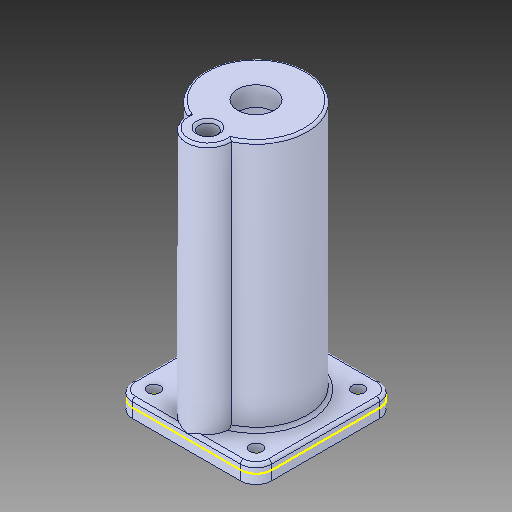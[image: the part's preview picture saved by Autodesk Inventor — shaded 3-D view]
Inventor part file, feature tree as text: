
AUTODESK INVENTOR PART (.ipt)
format: ipt  version: 2018 (Build 220112000, 112)  size: 358,912 bytes
history: native  units: in
note: dims shown in document units (in); Inventor stores cm internally (conversion verified against a paired STEP export)
features: extrude x16, sketch x13, projected_geometry x13, fillet x6, chamfer x1, revolve x1, other x1
ambient origin geometry x8: Origin, YZ Plane, XZ Plane, XY Plane, X Axis, Y Axis, Z Axis, Center Point
bodies: Solid1 (feature_tree)
feature tree (51):
  extrude  "Extrusion1"  TaperAngle=0.0deg  [1 undecoded]
  sketch  "Sketch2"  dims[d4=0.3937in d5=0.0in d6=1.0in d7=0.0in]
  extrude  "Extrusion2"  Depth=1.0in TaperAngle=0.0deg
  extrude  "Extrusion3"  Depth=0.9252in
  sketch  "Sketch3"  dims[d8=2.0in d9=0.0in d10=0.9252in]
  extrude  "Extrusion4"  Depth=2.0in TaperAngle=0.0deg
  extrude  "Extrusion5"  Depth=1.0in
  extrude  "Extrusion6"  Depth=0.3937in TaperAngle=0.0deg
  fillet  "Fillet2"  Radius=0.3937in
  fillet  "Fillet3"  Radius=0.45in
  sketch  "Sketch5"  dims[d14=0.5in d15=1.0in]
  extrude  "Extrusion7"  Depth=0.125in
  extrude  "Extrusion9"  TaperAngle=0.0deg  [1 undecoded]
  extrude  "Extrusion10"  Depth=0.9375in
  fillet  "Fillet4"  Radius=0.5in
  extrude  "Extrusion11"  Depth=0.0625in TaperAngle=45.0deg
  sketch  "Sketch9"  dims[d27=0.0in d28=0.0in d29=0.0in d30=0.0in]
  extrude  "Extrusion12"  Depth=0.25in TaperAngle=0.0deg
  extrude  "Extrusion13"  Depth=0.25in TaperAngle=0.0deg
  extrude  "Extrusion14"  Depth=1.374in
  fillet  "Fillet5"  [1 undecoded]
  chamfer  "Chamfer2"  [1 undecoded]
  fillet  "Fillet6"  [1 undecoded]
  sketch  "Sketch13"  dims[d46=0.25in d47=0.0in d48=0.25in d49=0.0in]
  extrude  "Extrusion15"  [1 undecoded]
  extrude  "Extrusion16"  [1 undecoded]
  extrude  "Extrusion17"  [1 undecoded]
  revolve  "Revolution1"  [1 undecoded]
  fillet  "Fillet1"  [1 undecoded]
  sketch  "Sketch1"  dims[d0=0.0in d1=0.0in d2=0.0in d3=0.0in]
  projected_geometry  "Projected Loop1"
  projected_geometry  "Projected Loop2"
  projected_geometry  "Projected Loop3"
  sketch  "Sketch4"  dims[d11=0.45in d12=2.0in d13=0.0in]
  projected_geometry  "Projected Loop4"
  sketch  "Sketch7"  dims[d16=1.0976in d17=0.3937in d18=0.0in d21=0.3937in d22=0.0in d23=0.45in]
  projected_geometry  "Projected Loop6"
  sketch  "Sketch8"  dims[d24=0.9843in d25=0.0in d26=0.125in]
  projected_geometry  "Projected Loop7"
  projected_geometry  "Projected Loop8"
  sketch  "Sketch10"  dims[d31=0.5in d32=0.0in d33=0.9375in d34=0.5in d35=0.0in]
  projected_geometry  "Projected Loop9"
  sketch  "Sketch11"  dims[d39=1.0in d40=0.0625in d41=0.0787in d42=45.0deg]
  projected_geometry  "Projected Loop10"
  sketch  "Sketch12"  dims[d43=0.0625in d44=0.25in d45=0.0in]
  projected_geometry  "Projected Loop11"
  sketch  "Sketch14"  dims[d51=0.125in d52=1.374in d53=90.0deg]
  projected_geometry  "Projected Loop12"
  projected_geometry  "Projected Loop13"
  projected_geometry  "Projected Loop14"
  other  "Ø8.0mm Dowel Hole1"
note: 10 required parameter values undecoded (feature->parameter linkage not recoverable at this tier; creation-order binding heuristic only, values carry confidence <= 0.55)
